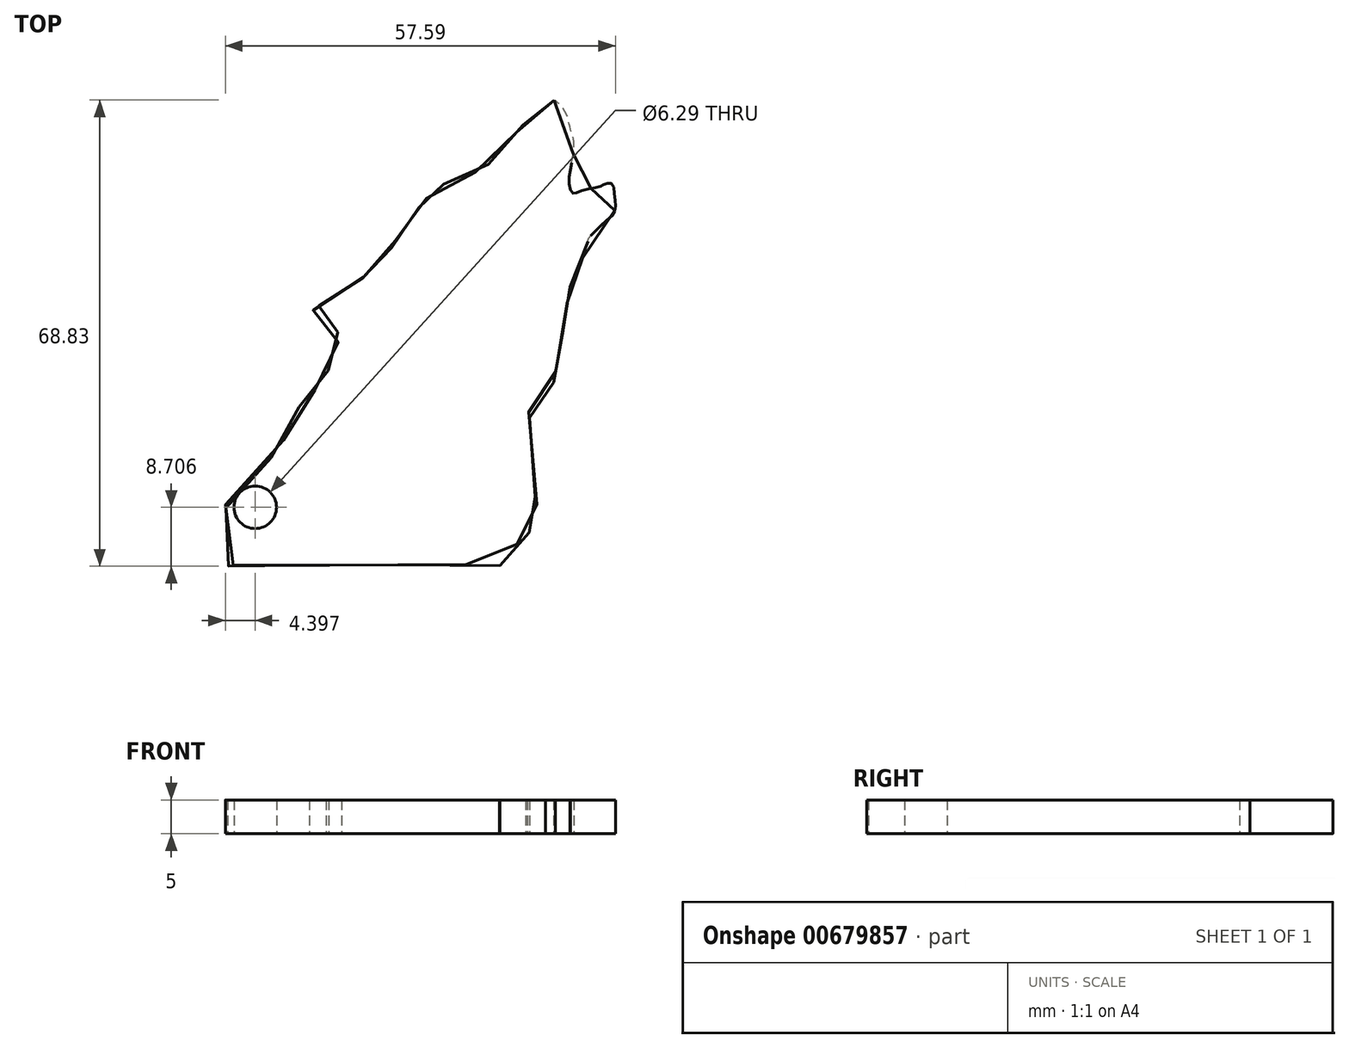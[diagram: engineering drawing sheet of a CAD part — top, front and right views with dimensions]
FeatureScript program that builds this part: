
annotation { "Feature Type Name" : "Feature", "Feature Type Description" : "" }
export const myFeature = defineFeature(function(context is Context, id is Id, definition is map)
    precondition{}
    {
        {
            var Q0;
            Q0=qCreatedBy(makeId("Top.planeOp"),FACE);
            var sketch = newSketch(context, id + "F0", { "sketchPlane" : qUnion([Q0])});
            skPoint(sketch, "E0.28.internal.snap0", {"position": v(-57.3, 34.32) * mm});
            skPoint(sketch, "E0.63.internal.snap0", {"position": v(-57.3, 34.32) * mm});
            skFitSpline(sketch, "E0", {"points": [v(-8.97, 68.64) * mm, v(-9.93, 68.44) * mm, v(-10.65, 67.9) * mm, v(-12.66, 65.99) * mm, v(-13.57, 64.96) * mm, v(-15.7, 62.5) * mm, v(-17.38, 60.45) * mm, v(-19.02, 58.9) * mm, v(-20.14, 58.2) * mm, v(-22.62, 57.3) * mm, v(-25.35, 56.24) * mm, v(-26.17, 55.82) * mm, v(-27.69, 54.37) * mm, v(-28.15, 53.74) * mm, v(-28.5, 53.4) * mm, v(-29.94, 51.14) * mm, v(-31.64, 48.65) * mm, v(-32.56, 47.68) * mm, v(-33.14, 46.47) * mm, v(-34.8, 44.82) * mm, v(-36.52, 43.17) * mm, v(-36.73, 42.82) * mm, v(-38.36, 41.7) * mm, v(-41.53, 39.57) * mm, v(-42.87, 38.84) * mm, v(-44.44, 37.7) * mm, v(-45.08, 37.02) * mm, v(-43.9, 35.76) * mm, v(-40.75, 34.32) * mm, v(-40.36, 33.72) * mm, v(-41.85, 31.75) * mm, v(-42.56, 29.4) * mm, v(-42.25, 28.3) * mm, v(-43.74, 26.4) * mm, v(-45, 25.23) * mm, v(-47.04, 22.71) * mm, v(-47.99, 20.9) * mm, v(-48.93, 18.47) * mm, v(-53.96, 12.73) * mm, v(-57.3, 10.06) * mm, v(-57.3, 7.46) * mm, v(-57.3, 2.75) * mm, v(-57.3, 0) * mm, v(-56.16, 0) * mm, v(-50.9, 0) * mm, v(-43.35, 0) * mm, v(-34.07, 0) * mm, v(-19.22, 0) * mm, v(-16.94, 0) * mm, v(-17.02, 0.7) * mm, v(-15.45, 1.88) * mm, v(-13.8, 3.93) * mm, v(-10.8, 6.05) * mm, v(-10.26, 6.76) * mm, v(-10.73, 6.84) * mm, v(-11.6, 9.59) * mm, v(-13.17, 16.97) * mm, v(-12.62, 21.93) * mm, v(-12.62, 24.44) * mm, v(-8.84, 25.94) * mm, v(-9, 27.04) * mm, v(-8.76, 28.3) * mm, v(-8.21, 33.48) * mm, v(-7.73, 34.32) * mm, v(-7.28, 37.73) * mm, v(-6.79, 39.11) * mm, v(-6.54, 39.7) * mm, v(-6.59, 41.4) * mm, v(-5.7, 44.31) * mm, v(-4.9, 45.1) * mm, v(-3.96, 47.83) * mm, v(-3.77, 48.37) * mm, v(-1.74, 50.4) * mm, v(0, 52.33) * mm, v(0, 54.37) * mm, v(-0.45, 56.35) * mm, v(-1.49, 56.25) * mm, v(-2.18, 55.9) * mm, v(-4.86, 55.3) * mm, v(-6.2, 54.9) * mm, v(-6.74, 56.6) * mm, v(-6.3, 59.86) * mm, v(-6.1, 63.08) * mm, v(-6.5, 64.17) * mm, v(-7.08, 66.45) * mm, v(-8.97, 68.64) * mm]});
            skCircle(sketch, "E1", {"center": v(-53.08, 8.56) * mm, "radius": 3.14 * mm});
            skSolve(sketch);
        }
        {
            var Q0;
            Q0 = qSketchRegion(id + "F0", true);
            extrude(context, id + "F1", {"entities" : qUnion([Q0]), "depth" : 5 * mm, "offsetDistance" : 25 * mm});
        }
        {
            var Q0;
            Q0=makeQuery(id+"F1.opExtrude","CAP_FACE",FACE,{"disambiguationData":[OSD([sQuery(id+"F0.wireOp",EDGE,"E0")])],"isStart":false});
            var sketch = newSketch(context, id + "F2", { "sketchPlane" : qUnion([Q0])});
            skCircle(sketch, "E2", {"center": v(-51.8, 8.37) * mm, "radius": 3.7 * mm});
            skSolve(sketch);
        }
        {
            var Q0;
            Q0 = qSketchRegion(id + "F2", true);
            extrude(context, id + "F3", {"entities" : qUnion([Q0]), "operationType" : NewBodyOperationType.REMOVE, "depth" : 5 * mm, "offsetDistance" : 25 * mm});
        }
        {
            var Q0;
            Q0 = qSketchRegion(id + "F0", true);
            extrude(context, id + "F4", {"entities" : qUnion([Q0]), "operationType" : NewBodyOperationType.REMOVE, "oppositeDirection" : true, "depth" : 5 * mm, "offsetDistance" : 25 * mm});
        }
    });
